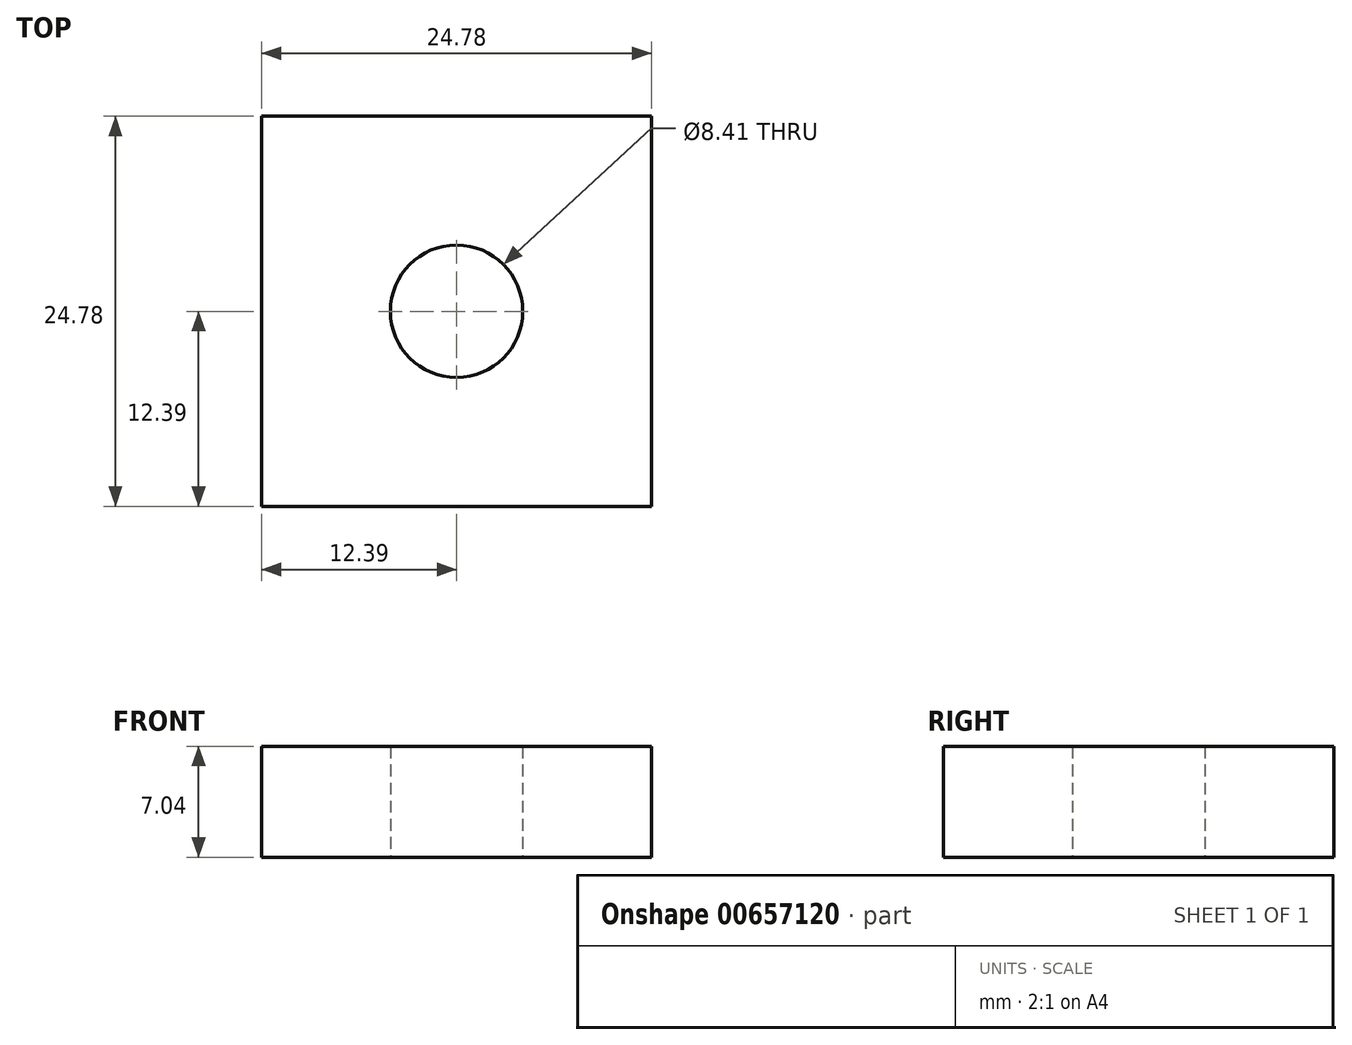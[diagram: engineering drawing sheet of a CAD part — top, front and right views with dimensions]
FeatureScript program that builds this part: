
annotation { "Feature Type Name" : "Feature", "Feature Type Description" : "" }
export const myFeature = defineFeature(function(context is Context, id is Id, definition is map)
    precondition{}
    {
        {
            var Q0;
            Q0=qCreatedBy(makeId("Top.planeOp"),FACE);
            var sketch = newSketch(context, id + "F0", { "sketchPlane" : qUnion([Q0])});
            skLineSegment(sketch, "E0.bottom", {"start": v(12.4, 12.4) * mm, "end": v(-12.4, 12.4) * mm});
            skLineSegment(sketch, "E0.top", {"start": v(12.4, -12.4) * mm, "end": v(-12.4, -12.4) * mm});
            skLineSegment(sketch, "E0.left", {"start": v(12.4, 12.4) * mm, "end": v(12.4, -12.4) * mm});
            skLineSegment(sketch, "E0.right", {"start": v(-12.4, 12.4) * mm, "end": v(-12.4, -12.4) * mm});
            skPoint(sketch, "E0.middle", {"position": v(0, 0) * mm});
            skCircle(sketch, "E1", {"center": v(0, 0) * mm, "radius": 4.2 * mm});
            skSolve(sketch);
        }
        {
            var Q0;
            Q0=makeQuery(id+"F0.imprint","IMPRINT",FACE,{"disambiguationData":[TD([[makeQuery(id+"F0.imprint","IMPRINT",EDGE,{"derivedFrom":sQuery(id+"F0.wireOp",EDGE,"E0.bottom")}),1.0]])]});
            extrude(context, id + "F1", {"entities" : qUnion([Q0]), "depth" : 7.04 * mm, "offsetDistance" : 25 * mm});
        }
    });
